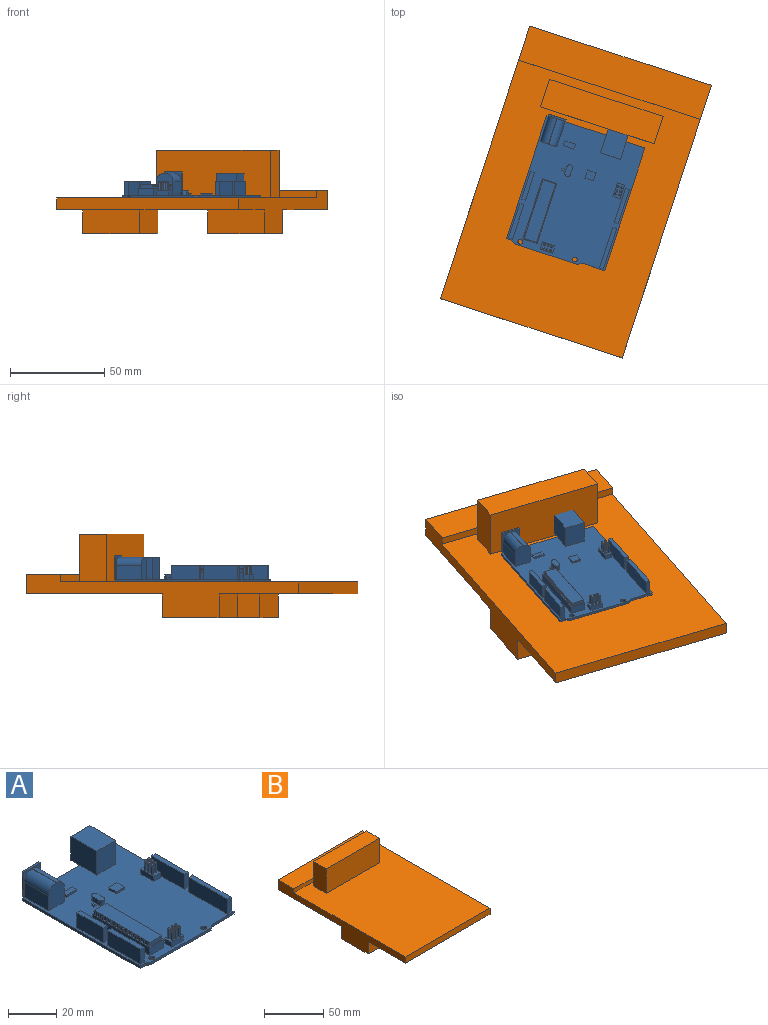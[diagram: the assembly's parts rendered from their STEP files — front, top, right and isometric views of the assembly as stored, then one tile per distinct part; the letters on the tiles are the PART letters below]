
ASSEMBLY  parts=2 mates=1
PART A: 244 faces, bbox 55x75.2x13.8 mm
  f0: plane 7x4mm, normal (0,0,1), area 23.3mm2, adj f194,f195,f196,f197,f226,f227,f228,f229
  f1: plane 7.5x4mm, normal (0,0,1), area 25.3mm2, adj f190,f191,f192,f193,f220,f221,f222,f223
  f2: plane 70x55mm, normal (0,0,1), area 3025.5mm2, adj f49,f50,f51,f52,f54,f55,f56,f57
  f3: plane 8.98x8.63mm, normal (0,1,0), area 52mm2, adj f179,f180,f181,f182,f183,f184,f185,f186
  f4: plane 1.5x0.4mm, normal (0,1,0), area 0.6mm2, adj f6,f46,f48,f178
  f5: plane 1.5x0.4mm, normal (0,-1,0), area 0.6mm2, adj f6,f46,f48,f178
  f6: plane 0.75x0.4mm, normal (0,0,1), area 0.3mm2, adj f4,f5,f46,f178
  f7: plane 1.5x0.4mm, normal (0,1,0), area 0.6mm2, adj f9,f46,f48,f177
  f8: plane 1.5x0.4mm, normal (0,-1,0), area 0.6mm2, adj f9,f46,f48,f177
  f9: plane 0.75x0.4mm, normal (0,0,1), area 0.3mm2, adj f7,f8,f46,f177
  f10: plane 1.5x0.4mm, normal (0,1,0), area 0.6mm2, adj f12,f46,f48,f176
  f11: plane 1.5x0.4mm, normal (0,-1,0), area 0.6mm2, adj f12,f46,f48,f176
  f12: plane 0.75x0.4mm, normal (0,0,1), area 0.3mm2, adj f10,f11,f46,f176
  f13: plane 1.5x0.4mm, normal (0,1,0), area 0.6mm2, adj f15,f46,f48,f175
  f14: plane 1.5x0.4mm, normal (0,-1,0), area 0.6mm2, adj f15,f46,f48,f175
  f15: plane 0.75x0.4mm, normal (0,0,1), area 0.3mm2, adj f13,f14,f46,f175
  f16: plane 1.5x0.4mm, normal (0,1,0), area 0.6mm2, adj f18,f46,f48,f174
  f17: plane 1.5x0.4mm, normal (0,-1,0), area 0.6mm2, adj f18,f46,f48,f174
  f18: plane 0.75x0.4mm, normal (0,0,1), area 0.3mm2, adj f16,f17,f46,f174
  f19: plane 1.5x0.4mm, normal (0,1,0), area 0.6mm2, adj f21,f46,f48,f173
  f20: plane 1.5x0.4mm, normal (0,-1,0), area 0.6mm2, adj f21,f46,f48,f173
  f21: plane 0.75x0.4mm, normal (0,0,1), area 0.3mm2, adj f19,f20,f46,f173
  f22: plane 1.5x0.4mm, normal (0,1,0), area 0.6mm2, adj f24,f46,f48,f172
  f23: plane 1.5x0.4mm, normal (0,-1,0), area 0.6mm2, adj f24,f46,f48,f172
  f24: plane 0.75x0.4mm, normal (0,0,1), area 0.3mm2, adj f22,f23,f46,f172
  f25: plane 1.5x0.4mm, normal (0,1,0), area 0.6mm2, adj f27,f46,f48,f171
  f26: plane 1.5x0.4mm, normal (0,-1,0), area 0.6mm2, adj f27,f46,f48,f171
  f27: plane 0.75x0.4mm, normal (0,0,1), area 0.3mm2, adj f25,f26,f46,f171
  f28: plane 1.5x0.4mm, normal (0,1,0), area 0.6mm2, adj f30,f46,f48,f170
  f29: plane 1.5x0.4mm, normal (0,-1,0), area 0.6mm2, adj f30,f46,f48,f170
  f30: plane 0.75x0.4mm, normal (0,0,1), area 0.3mm2, adj f28,f29,f46,f170
  f31: plane 1.5x0.4mm, normal (0,1,0), area 0.6mm2, adj f33,f46,f48,f169
  f32: plane 1.5x0.4mm, normal (0,-1,0), area 0.6mm2, adj f33,f46,f48,f169
  f33: plane 0.75x0.4mm, normal (0,0,1), area 0.3mm2, adj f31,f32,f46,f169
  f34: plane 1.5x0.4mm, normal (0,1,0), area 0.6mm2, adj f36,f46,f48,f168
  f35: plane 1.5x0.4mm, normal (0,-1,0), area 0.6mm2, adj f36,f46,f48,f168
  f36: plane 0.75x0.4mm, normal (0,0,1), area 0.3mm2, adj f34,f35,f46,f168
  f37: plane 1.5x0.4mm, normal (0,1,0), area 0.6mm2, adj f39,f46,f48,f167
  f38: plane 1.5x0.4mm, normal (0,-1,0), area 0.6mm2, adj f39,f46,f48,f167
  f39: plane 0.75x0.4mm, normal (0,0,1), area 0.3mm2, adj f37,f38,f46,f167
  f40: plane 1.5x0.4mm, normal (0,1,0), area 0.6mm2, adj f42,f46,f48,f166
  f41: plane 1.5x0.4mm, normal (0,-1,0), area 0.6mm2, adj f42,f46,f48,f166
  f42: plane 0.75x0.4mm, normal (0,0,1), area 0.3mm2, adj f40,f41,f46,f166
  f43: plane 1.5x0.4mm, normal (0,1,0), area 0.6mm2, adj f45,f46,f48,f165
  f44: plane 1.5x0.4mm, normal (0,-1,0), area 0.6mm2, adj f45,f46,f48,f165
  f45: plane 0.75x0.4mm, normal (0,0,1), area 0.3mm2, adj f43,f44,f46,f165
  f46: plane 32.63x2mm, normal (1,0,0), area 49.5mm2, adj f4,f5,f6,f7,f8,f9,f10,f11
  f47: plane 32.63x2mm, normal (-1,0,0), area 49.5mm2, adj f48,f106,f107,f108,f109,f110,f111,f112
  f48: plane 33.63x7.95mm, normal (0,0,1), area 32.2mm2, adj f4,f5,f7,f8,f10,f11,f13,f14
  f49: plane 33.63x4mm, normal (-1,0,0), area 134.5mm2, adj f2,f48,f50,f52
  f50: plane 7.95x4mm, normal (0,-1,0), area 31.8mm2, adj f2,f48,f49,f51
  f51: plane 33.63x4mm, normal (1,0,0), area 134.5mm2, adj f2,f48,f50,f52
  f52: plane 7.95x4mm, normal (0,1,0), area 31.8mm2, adj f2,f48,f49,f51
  f53: plane 6.98x6.98mm, normal (0,1,0), area 37.5mm2, adj f103,f104
  f54: plane 68.67x1.25mm, normal (1,0,0), area 85.8mm2, adj f2,f55,f58,f95
  f55: plane 55x1.25mm, normal (0,1,0), area 68.8mm2, adj f2,f54,f56,f58,f79,f84
  f56: plane 68.67x1.25mm, normal (-1,0,0), area 85.8mm2, adj f2,f55,f58,f92
  f57: plane 35.3x1.25mm, normal (0,-1,0), area 44.1mm2, adj f2,f58,f93,f94
  f58: plane 70x55mm, normal (0,0,-1), area 3816.6mm2, adj f54,f55,f56,f57,f92,f93,f94,f95
  f59: plane 7.5x2.22mm, normal (0,-1,0), area 16.7mm2, adj f2,f60,f62,f63
  f60: plane 22.58x7.5mm, normal (1,0,0), area 169.3mm2, adj f2,f59,f61,f63
  f61: plane 7.5x2.22mm, normal (0,1,0), area 16.7mm2, adj f2,f60,f62,f63
  f62: plane 22.58x7.5mm, normal (-1,0,0), area 169.3mm2, adj f2,f59,f61,f63
  f63: plane 22.58x2.22mm, normal (0,0,1), area 50.1mm2, adj f59,f60,f61,f62
  f64: plane 19.27x7.5mm, normal (-1,0,0), area 144.5mm2, adj f2,f65,f67,f68
  f65: plane 7.5x2.22mm, normal (0,-1,0), area 16.7mm2, adj f2,f64,f66,f68
  f66: plane 19.27x7.5mm, normal (1,0,0), area 144.5mm2, adj f2,f65,f67,f68
  f67: plane 7.5x2.22mm, normal (0,1,0), area 16.7mm2, adj f2,f64,f66,f68
  f68: plane 19.27x2.22mm, normal (0,0,1), area 42.8mm2, adj f64,f65,f66,f67
  f69: plane 19.1x7.5mm, normal (-1,0,0), area 143.2mm2, adj f2,f70,f72,f73
  f70: plane 7.5x2.22mm, normal (0,-1,0), area 16.7mm2, adj f2,f69,f71,f73
  f71: plane 19.1x7.5mm, normal (1,0,0), area 143.2mm2, adj f2,f70,f72,f73
  f72: plane 7.5x2.22mm, normal (0,1,0), area 16.7mm2, adj f2,f69,f71,f73
  f73: plane 19.1x2.22mm, normal (0,0,1), area 42.4mm2, adj f69,f70,f71,f72
  f74: plane 15.53x7.5mm, normal (1,0,0), area 116.5mm2, adj f2,f75,f77,f78
  f75: plane 7.5x2.22mm, normal (0,1,0), area 16.7mm2, adj f2,f74,f76,f78
  f76: plane 15.53x7.5mm, normal (-1,0,0), area 116.5mm2, adj f2,f75,f77,f78
  f77: plane 7.5x2.22mm, normal (0,-1,0), area 16.7mm2, adj f2,f74,f76,f78
  f78: plane 15.53x2.22mm, normal (0,0,1), area 34.5mm2, adj f74,f75,f76,f77
  f79: plane 9.89x1.2mm, normal (0,0,-1), area 11.7mm2, adj f55,f80,f82,f98,f99,f101,f102
  f80: plane 14.15x7.5mm, normal (-1,0,0), area 106.1mm2, adj f2,f79,f81,f90,f98
  f81: plane 12x9.24mm, normal (0,-1,0), area 102.2mm2, adj f2,f80,f82,f83,f90,f91
  f82: plane 14.15x7.5mm, normal (1,0,0), area 106.1mm2, adj f2,f79,f81,f91,f98
  f83: plane 14.15x0.24mm, normal (0,0,1), area 3.4mm2, adj f81,f90,f91,f98
  f84: plane 11.11x5.16mm, normal (0,0,-1), area 57.3mm2, adj f55,f85,f87,f88
  f85: plane 15.05x12mm, normal (-1,0,0), area 180.6mm2, adj f2,f84,f86,f88,f89
  f86: plane 12x11.11mm, normal (0,-1,0), area 133.3mm2, adj f2,f85,f87,f89
  f87: plane 15.05x12mm, normal (1,0,0), area 180.6mm2, adj f2,f84,f86,f88,f89
  f88: plane 12x11.11mm, normal (0,1,0), area 60.1mm2, adj f84,f85,f87,f89,f179,f180,f181,f182
  f89: plane 15.05x11.11mm, normal (0,0,1), area 167.2mm2, adj f85,f86,f87,f88
  f90: cylinder r=4.5mm len=14.15mm, axis (0,1,0), area 100mm2, adj f80,f81,f83,f98
  f91: cylinder r=4.5mm len=14.15mm, axis (0,-1,0), area 100mm2, adj f81,f82,f83,f98
  f92: plane 2.98x1.25mm, normal (0,-1,0), area 3.7mm2, adj f2,f56,f58,f93
  f93: plane 2.01x1.33mm, normal (-0.55,-0.83,0), area 3mm2, adj f2,f57,f58,f92
  f94: plane 2.01x1.33mm, normal (0.55,-0.83,0), area 3mm2, adj f2,f57,f58,f95
  f95: plane 12.71x1.25mm, normal (0,-1,0), area 15.9mm2, adj f2,f54,f58,f94
  f96: cylinder r=1.25mm len=2.5mm, axis (0,0,1), area 9.8mm2, adj f2,f58
  f97: cylinder r=1.25mm len=2.5mm, axis (0,0,1), area 9.8mm2, adj f2,f58
  f98: plane 12.57x9.89mm, normal (0,-1,0), area 22.1mm2, adj f79,f80,f82,f83,f90,f91,f99,f100
  f99: plane 12.57x1mm, normal (-1,0,0), area 12.6mm2, adj f79,f98,f100,f102
  f100: plane 9.89x1mm, normal (0,0,1), area 9.9mm2, adj f98,f99,f101,f102
  f101: plane 12.57x1mm, normal (1,0,0), area 12.6mm2, adj f79,f98,f100,f102
  f102: plane 12.57x9.89mm, normal (0,1,0), area 86mm2, adj f79,f99,f100,f101,f103
  f103: cylinder r=3.49mm len=12mm, axis (0,1,0), area 263.3mm2, adj f53,f102
  f104: cylinder r=0.5mm len=8mm, axis (0,-1,0), area 25.1mm2, adj f53,f105
  f105: plane 1x1mm, normal (0,1,0), area 0.8mm2, adj f104
  f106: plane 6.95x2mm, normal (0,1,0), area 13.9mm2, adj f46,f47,f48,f108
  f107: plane 6.95x2mm, normal (0,-1,0), area 13.9mm2, adj f46,f47,f48,f108
  f108: plane 32.63x6.95mm, normal (0,0,1), area 226.7mm2, adj f46,f47,f106,f107
  f109: plane 1.5x0.4mm, normal (0,1,0), area 0.6mm2, adj f47,f48,f111,f164
  f110: plane 1.5x0.4mm, normal (0,-1,0), area 0.6mm2, adj f47,f48,f111,f164
  f111: plane 0.75x0.4mm, normal (0,0,1), area 0.3mm2, adj f47,f109,f110,f164
  f112: plane 1.5x0.4mm, normal (0,1,0), area 0.6mm2, adj f47,f48,f114,f163
  f113: plane 1.5x0.4mm, normal (0,-1,0), area 0.6mm2, adj f47,f48,f114,f163
  f114: plane 0.75x0.4mm, normal (0,0,1), area 0.3mm2, adj f47,f112,f113,f163
  f115: plane 1.5x0.4mm, normal (0,1,0), area 0.6mm2, adj f47,f48,f117,f162
  f116: plane 1.5x0.4mm, normal (0,-1,0), area 0.6mm2, adj f47,f48,f117,f162
  f117: plane 0.75x0.4mm, normal (0,0,1), area 0.3mm2, adj f47,f115,f116,f162
  f118: plane 1.5x0.4mm, normal (0,1,0), area 0.6mm2, adj f47,f48,f120,f161
  f119: plane 1.5x0.4mm, normal (0,-1,0), area 0.6mm2, adj f47,f48,f120,f161
  f120: plane 0.75x0.4mm, normal (0,0,1), area 0.3mm2, adj f47,f118,f119,f161
  f121: plane 1.5x0.4mm, normal (0,1,0), area 0.6mm2, adj f47,f48,f123,f160
  f122: plane 1.5x0.4mm, normal (0,-1,0), area 0.6mm2, adj f47,f48,f123,f160
  f123: plane 0.75x0.4mm, normal (0,0,1), area 0.3mm2, adj f47,f121,f122,f160
  f124: plane 1.5x0.4mm, normal (0,1,0), area 0.6mm2, adj f47,f48,f126,f159
  f125: plane 1.5x0.4mm, normal (0,-1,0), area 0.6mm2, adj f47,f48,f126,f159
  f126: plane 0.75x0.4mm, normal (0,0,1), area 0.3mm2, adj f47,f124,f125,f159
  f127: plane 1.5x0.4mm, normal (0,1,0), area 0.6mm2, adj f47,f48,f129,f158
  f128: plane 1.5x0.4mm, normal (0,-1,0), area 0.6mm2, adj f47,f48,f129,f158
  f129: plane 0.75x0.4mm, normal (0,0,1), area 0.3mm2, adj f47,f127,f128,f158
  f130: plane 1.5x0.4mm, normal (0,1,0), area 0.6mm2, adj f47,f48,f132,f157
  f131: plane 1.5x0.4mm, normal (0,-1,0), area 0.6mm2, adj f47,f48,f132,f157
  f132: plane 0.75x0.4mm, normal (0,0,1), area 0.3mm2, adj f47,f130,f131,f157
  f133: plane 1.5x0.4mm, normal (0,1,0), area 0.6mm2, adj f47,f48,f135,f156
  f134: plane 1.5x0.4mm, normal (0,-1,0), area 0.6mm2, adj f47,f48,f135,f156
  f135: plane 0.75x0.4mm, normal (0,0,1), area 0.3mm2, adj f47,f133,f134,f156
  f136: plane 1.5x0.4mm, normal (0,1,0), area 0.6mm2, adj f47,f48,f138,f155
  f137: plane 1.5x0.4mm, normal (0,-1,0), area 0.6mm2, adj f47,f48,f138,f155
  f138: plane 0.75x0.4mm, normal (0,0,1), area 0.3mm2, adj f47,f136,f137,f155
  f139: plane 1.5x0.4mm, normal (0,1,0), area 0.6mm2, adj f47,f48,f141,f154
  f140: plane 1.5x0.4mm, normal (0,-1,0), area 0.6mm2, adj f47,f48,f141,f154
  f141: plane 0.75x0.4mm, normal (0,0,1), area 0.3mm2, adj f47,f139,f140,f154
  f142: plane 1.5x0.4mm, normal (0,1,0), area 0.6mm2, adj f47,f48,f144,f153
  f143: plane 1.5x0.4mm, normal (0,-1,0), area 0.6mm2, adj f47,f48,f144,f153
  f144: plane 0.75x0.4mm, normal (0,0,1), area 0.3mm2, adj f47,f142,f143,f153
  f145: plane 1.5x0.4mm, normal (0,1,0), area 0.6mm2, adj f47,f48,f147,f152
  f146: plane 1.5x0.4mm, normal (0,-1,0), area 0.6mm2, adj f47,f48,f147,f152
  f147: plane 0.75x0.4mm, normal (0,0,1), area 0.3mm2, adj f47,f145,f146,f152
  f148: plane 1.5x0.4mm, normal (0,1,0), area 0.6mm2, adj f47,f48,f150,f151
  f149: plane 1.5x0.4mm, normal (0,-1,0), area 0.6mm2, adj f47,f48,f150,f151
  f150: plane 0.75x0.4mm, normal (0,0,1), area 0.3mm2, adj f47,f148,f149,f151
  f151: plane 1.5x0.75mm, normal (-1,0,0), area 1.1mm2, adj f48,f148,f149,f150
  f152: plane 1.5x0.75mm, normal (-1,0,0), area 1.1mm2, adj f48,f145,f146,f147
  f153: plane 1.5x0.75mm, normal (-1,0,0), area 1.1mm2, adj f48,f142,f143,f144
  f154: plane 1.5x0.75mm, normal (-1,0,0), area 1.1mm2, adj f48,f139,f140,f141
  f155: plane 1.5x0.75mm, normal (-1,0,0), area 1.1mm2, adj f48,f136,f137,f138
  f156: plane 1.5x0.75mm, normal (-1,0,0), area 1.1mm2, adj f48,f133,f134,f135
  f157: plane 1.5x0.75mm, normal (-1,0,0), area 1.1mm2, adj f48,f130,f131,f132
  f158: plane 1.5x0.75mm, normal (-1,0,0), area 1.1mm2, adj f48,f127,f128,f129
  f159: plane 1.5x0.75mm, normal (-1,0,0), area 1.1mm2, adj f48,f124,f125,f126
  f160: plane 1.5x0.75mm, normal (-1,0,0), area 1.1mm2, adj f48,f121,f122,f123
  f161: plane 1.5x0.75mm, normal (-1,0,0), area 1.1mm2, adj f48,f118,f119,f120
  f162: plane 1.5x0.75mm, normal (-1,0,0), area 1.1mm2, adj f48,f115,f116,f117
  f163: plane 1.5x0.75mm, normal (-1,0,0), area 1.1mm2, adj f48,f112,f113,f114
  f164: plane 1.5x0.75mm, normal (-1,0,0), area 1.1mm2, adj f48,f109,f110,f111
  f165: plane 1.5x0.75mm, normal (1,0,0), area 1.1mm2, adj f43,f44,f45,f48
  f166: plane 1.5x0.75mm, normal (1,0,0), area 1.1mm2, adj f40,f41,f42,f48
  f167: plane 1.5x0.75mm, normal (1,0,0), area 1.1mm2, adj f37,f38,f39,f48
  f168: plane 1.5x0.75mm, normal (1,0,0), area 1.1mm2, adj f34,f35,f36,f48
  f169: plane 1.5x0.75mm, normal (1,0,0), area 1.1mm2, adj f31,f32,f33,f48
  f170: plane 1.5x0.75mm, normal (1,0,0), area 1.1mm2, adj f28,f29,f30,f48
  f171: plane 1.5x0.75mm, normal (1,0,0), area 1.1mm2, adj f25,f26,f27,f48
  f172: plane 1.5x0.75mm, normal (1,0,0), area 1.1mm2, adj f22,f23,f24,f48
  f173: plane 1.5x0.75mm, normal (1,0,0), area 1.1mm2, adj f19,f20,f21,f48
  f174: plane 1.5x0.75mm, normal (1,0,0), area 1.1mm2, adj f16,f17,f18,f48
  f175: plane 1.5x0.75mm, normal (1,0,0), area 1.1mm2, adj f13,f14,f15,f48
  f176: plane 1.5x0.75mm, normal (1,0,0), area 1.1mm2, adj f10,f11,f12,f48
  f177: plane 1.5x0.75mm, normal (1,0,0), area 1.1mm2, adj f7,f8,f9,f48
  f178: plane 1.5x0.75mm, normal (1,0,0), area 1.1mm2, adj f4,f5,f6,f48
  f179: plane 10x6.73mm, normal (1,0,0), area 67.3mm2, adj f3,f88,f180,f184
  f180: plane 10x8.63mm, normal (0,0,1), area 86.3mm2, adj f3,f88,f179,f181
  f181: plane 10x6.73mm, normal (-1,0,0), area 67.3mm2, adj f3,f88,f180,f182
  f182: plane 10x2.24mm, normal (-0.76,0,-0.65), area 29.4mm2, adj f3,f88,f181,f183
  f183: plane 10x4.83mm, normal (0,0,-1), area 48.3mm2, adj f3,f88,f182,f184
  f184: plane 10x2.24mm, normal (0.76,0,-0.65), area 29.4mm2, adj f3,f88,f179,f183
  f185: plane 8x3.45mm, normal (-1,0,0), area 27.6mm2, adj f3,f186,f188,f189
  f186: plane 8x6.13mm, normal (0,0,1), area 49mm2, adj f3,f185,f187,f189
  f187: plane 8x3.45mm, normal (1,0,0), area 27.6mm2, adj f3,f186,f188,f189
  f188: plane 8x6.13mm, normal (0,0,-1), area 49mm2, adj f3,f185,f187,f189
  f189: plane 6.13x3.45mm, normal (0,1,0), area 21.2mm2, adj f185,f186,f187,f188
  f190: plane 7.5x2.5mm, normal (-1,0,0), area 18.7mm2, adj f1,f2,f191,f193
  f191: plane 4x2.5mm, normal (0,-1,0), area 10mm2, adj f1,f2,f190,f192
  f192: plane 7.5x2.5mm, normal (1,0,0), area 18.7mm2, adj f1,f2,f191,f193
  f193: plane 4x2.5mm, normal (0,1,0), area 10mm2, adj f1,f2,f190,f192
  f194: plane 4x2.5mm, normal (-1,0,0), area 10mm2, adj f0,f2,f195,f197
  f195: plane 7x2.5mm, normal (0,-1,0), area 17.5mm2, adj f0,f2,f194,f196
  f196: plane 4x2.5mm, normal (1,0,0), area 10mm2, adj f0,f2,f195,f197
  f197: plane 7x2.5mm, normal (0,1,0), area 17.5mm2, adj f0,f2,f194,f196
  f198: plane 3.5x2.5mm, normal (-1,0,0), area 8.8mm2, adj f2,f200,f201,f203
  f199: plane 3.5x2.5mm, normal (1,0,0), area 8.8mm2, adj f2,f200,f202,f204
  f200: plane 6.5x3mm, normal (0,0,1), area 17.6mm2, adj f198,f199,f201,f202,f203,f204
  f201: cylinder r=1.5mm len=2.5mm, axis (0,0,-1), area 5.9mm2, adj f2,f198,f200,f202
  f202: cylinder r=1.5mm len=2.5mm, axis (0,0,-1), area 5.9mm2, adj f2,f199,f200,f201
  f203: cylinder r=1.5mm len=2.5mm, axis (0,0,-1), area 5.9mm2, adj f2,f198,f200,f204
  f204: cylinder r=1.5mm len=2.5mm, axis (0,0,-1), area 5.9mm2, adj f2,f199,f200,f203
  f205: plane 2.66x1mm, normal (-1,0,0), area 2.7mm2, adj f2,f206,f208,f209
  f206: plane 5.95x1mm, normal (0,-1,0), area 6mm2, adj f2,f205,f207,f209
  f207: plane 2.66x1mm, normal (1,0,0), area 2.7mm2, adj f2,f206,f208,f209
  f208: plane 5.95x1mm, normal (0,1,0), area 6mm2, adj f2,f205,f207,f209
  f209: plane 5.95x2.66mm, normal (0,0,1), area 15.9mm2, adj f205,f206,f207,f208
  f210: plane 1.1x1mm, normal (-1,0,0), area 1.1mm2, adj f2,f211,f213,f214
  f211: plane 1.57x1mm, normal (0,-1,0), area 1.6mm2, adj f2,f210,f212,f214
  f212: plane 1.1x1mm, normal (1,0,0), area 1.1mm2, adj f2,f211,f213,f214
  f213: plane 1.57x1mm, normal (0,1,0), area 1.6mm2, adj f2,f210,f212,f214
  f214: plane 1.57x1.1mm, normal (0,0,1), area 1.7mm2, adj f210,f211,f212,f213
  f215: plane 4.54x1mm, normal (-1,0,0), area 4.5mm2, adj f2,f216,f218,f219
  f216: plane 4.86x1mm, normal (0,-1,0), area 4.9mm2, adj f2,f215,f217,f219
  f217: plane 4.54x1mm, normal (1,0,0), area 4.5mm2, adj f2,f216,f218,f219
  f218: plane 4.86x1mm, normal (0,1,0), area 4.9mm2, adj f2,f215,f217,f219
  f219: plane 4.86x4.54mm, normal (0,0,1), area 22.1mm2, adj f215,f216,f217,f218
  f220: cylinder r=0.5mm len=4.5mm, axis (0,0,-1), area 14.1mm2, adj f1,f237
  f221: cylinder r=0.5mm len=4.5mm, axis (0,0,-1), area 14.1mm2, adj f1,f238
  f222: cylinder r=0.5mm len=4.5mm, axis (0,0,-1), area 14.1mm2, adj f1,f235
  f223: cylinder r=0.5mm len=4.5mm, axis (0,0,-1), area 14.1mm2, adj f1,f232
  f224: cylinder r=0.5mm len=4.5mm, axis (0,0,-1), area 14.1mm2, adj f1,f233
  f225: cylinder r=0.5mm len=4.5mm, axis (0,0,-1), area 14.1mm2, adj f1,f234
  f226: cylinder r=0.5mm len=4.5mm, axis (0,0,-1), area 14.1mm2, adj f0,f239
  f227: cylinder r=0.5mm len=4.5mm, axis (0,0,-1), area 14.1mm2, adj f0,f236
  f228: cylinder r=0.5mm len=4.5mm, axis (0,0,-1), area 14.1mm2, adj f0,f242
  f229: cylinder r=0.5mm len=4.5mm, axis (0,0,-1), area 14.1mm2, adj f0,f241
  f230: cylinder r=0.5mm len=4.5mm, axis (0,0,-1), area 14.1mm2, adj f0,f240
  f231: cylinder r=0.5mm len=4.5mm, axis (0,0,-1), area 14.1mm2, adj f0,f243
  f232: sphere r=0.5mm, area 1.6mm2, adj f223
  f233: sphere r=0.5mm, area 1.6mm2, adj f224
  f234: sphere r=0.5mm, area 1.6mm2, adj f225
  f235: sphere r=0.5mm, area 1.6mm2, adj f222
  f236: sphere r=0.5mm, area 1.6mm2, adj f227
  f237: sphere r=0.5mm, area 1.6mm2, adj f220
  f238: sphere r=0.5mm, area 1.6mm2, adj f221
  f239: sphere r=0.5mm, area 1.6mm2, adj f226
  f240: sphere r=0.5mm, area 1.6mm2, adj f230
  f241: sphere r=0.5mm, area 1.6mm2, adj f229
  f242: sphere r=0.5mm, area 1.6mm2, adj f228
  f243: sphere r=0.5mm, area 1.6mm2, adj f231
PART B: 21 faces, bbox 101.6x152.4x44.5 mm
  f0: plane 101.6x10.32mm, normal (0,1,0), area 1048.4mm2, adj f1,f3,f5,f12
  f1: plane 152.4x23.02mm, normal (-1,0,0), area 1446.6mm2, adj f0,f2,f4,f5,f11,f12,f13,f14
  f2: plane 101.6x6.35mm, normal (0,-1,0), area 645.2mm2, adj f1,f3,f4,f5
  f3: plane 152.4x23.02mm, normal (1,0,0), area 1446.6mm2, adj f0,f2,f4,f5,f11,f12,f17,f19
  f4: plane 133.35x101.6mm, normal (0,0,1), area 12573.7mm2, adj f1,f2,f3,f6,f7,f8,f9,f11
  f5: plane 152.4x101.6mm, normal (0,0,-1), area 13467.7mm2, adj f0,f1,f2,f3,f13,f14,f15,f17
  f6: plane 25.4x15.35mm, normal (-1,0,0), area 389.9mm2, adj f4,f7,f9,f10
  f7: plane 63.5x25.4mm, normal (0,-1,0), area 1612.9mm2, adj f4,f6,f8,f10
  f8: plane 25.4x15.35mm, normal (1,0,0), area 389.9mm2, adj f4,f7,f9,f10
  f9: plane 63.5x25.4mm, normal (0,1,0), area 1612.9mm2, adj f4,f6,f8,f10
  f10: plane 63.5x15.35mm, normal (0,0,1), area 974.7mm2, adj f6,f7,f8,f9
  f11: plane 101.6x3.97mm, normal (0,-1,0), area 403.2mm2, adj f1,f3,f4,f12
  f12: plane 101.6x19.05mm, normal (0,0,1), area 1935.5mm2, adj f0,f1,f3,f11
  f13: plane 31.75x12.7mm, normal (0,-1,0), area 403.2mm2, adj f1,f5,f15,f16
  f14: plane 31.75x12.7mm, normal (0,1,0), area 403.2mm2, adj f1,f5,f15,f16
  f15: plane 31.75x12.7mm, normal (1,0,0), area 403.2mm2, adj f5,f13,f14,f16
  f16: plane 31.75x31.75mm, normal (0,0,-1), area 1008.1mm2, adj f1,f13,f14,f15
  f17: plane 31.75x12.7mm, normal (0,-1,0), area 403.2mm2, adj f3,f5,f18,f20
  f18: plane 31.75x12.7mm, normal (-1,0,0), area 403.2mm2, adj f5,f17,f19,f20
  f19: plane 31.75x12.7mm, normal (0,1,0), area 403.2mm2, adj f3,f5,f18,f20
  f20: plane 31.75x31.75mm, normal (0,0,-1), area 1008.1mm2, adj f3,f17,f18,f19
PLACE A rot(axis=(0,0,-1),18.1deg) t=(95.46,23.54,76.16)mm
PLACE B rot(axis=(0,0,-1),18.1deg) t=(23.88,-31.85,69.81)mm
MATE fastened B.f4 <-> A.f58  axis (0,0,1) through (91.57,11.76,76.16)mm
